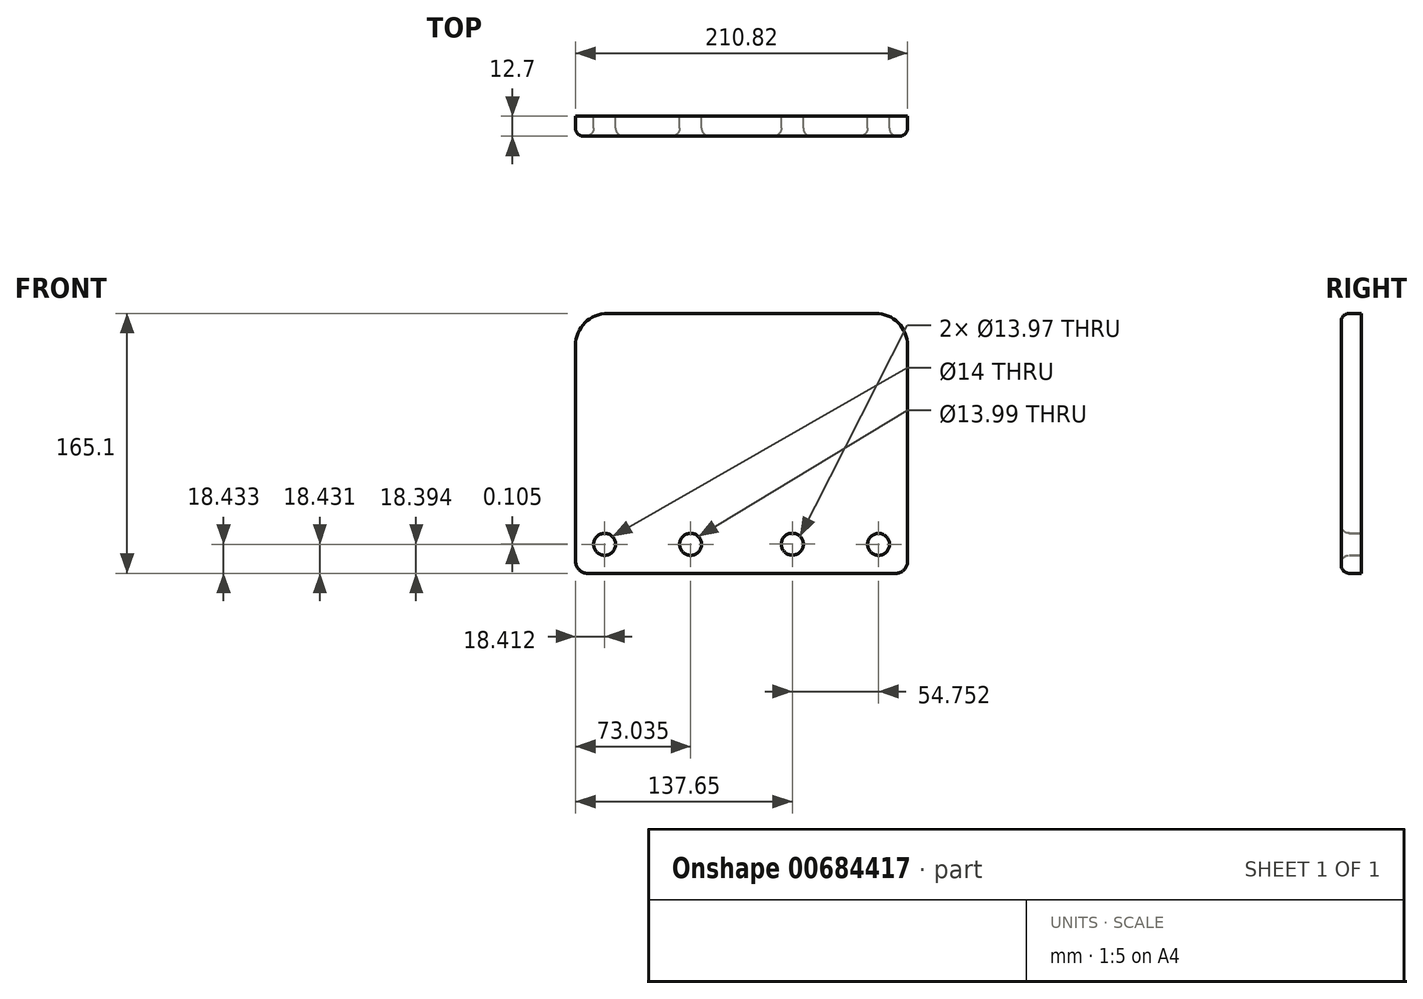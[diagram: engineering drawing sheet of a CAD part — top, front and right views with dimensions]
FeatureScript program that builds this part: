
annotation { "Feature Type Name" : "Feature", "Feature Type Description" : "" }
export const myFeature = defineFeature(function(context is Context, id is Id, definition is map)
    precondition{}
    {
        {
            var Q0;
            Q0=qCreatedBy(makeId("Front.planeOp"),FACE);
            var sketch = newSketch(context, id + "F0", { "sketchPlane" : qUnion([Q0])});
            skArc(sketch, "E0.7", {"start": v(-132.5, 111.2) * mm, "mid": v(-146.87, 105.25) * mm, "end": v(-152.82, 90.88) * mm});
            skLineSegment(sketch, "E0.8", {"start": v(-152.82, 90.88) * mm, "end": v(-152.82, -46.28) * mm});
            skLineSegment(sketch, "E0.9", {"start": v(-145.2, -53.9) * mm, "end": v(-55.03, -53.9) * mm});
            skArc(sketch, "E1.1", {"start": v(58, 90.88) * mm, "mid": v(52.05, 105.25) * mm, "end": v(37.68, 111.2) * mm});
            skLineSegment(sketch, "E1.2", {"start": v(58, -46.28) * mm, "end": v(58, 90.88) * mm});
            skLineSegment(sketch, "E1.3", {"start": v(-39.79, -53.9) * mm, "end": v(50.38, -53.9) * mm});
            skLineSegment(sketch, "E2", {"start": v(-55.03, -53.9) * mm, "end": v(-39.79, -53.9) * mm});
            skPoint(sketch, "E3.orphan", {"position": v(-98, 109.82) * mm});
            skLineSegment(sketch, "E4", {"start": v(21.17, 85.8) * mm, "end": v(21.17, 85.8) * mm});
            skLineSegment(sketch, "E5", {"start": v(-115.99, 85.8) * mm, "end": v(-115.99, 85.8) * mm});
            skPoint(sketch, "E6.visualSharp", {"position": v(-108.37, 111.2) * mm});
            skPoint(sketch, "E7.visualSharp", {"position": v(-108.37, 85.8) * mm});
            skPoint(sketch, "E8.newPointB", {"position": v(-121.07, 102.31) * mm});
            skPoint(sketch, "E9.visualSharp", {"position": v(13.55, 111.2) * mm});
            skPoint(sketch, "E10.orphan", {"position": v(26.25, 102.31) * mm});
            skPoint(sketch, "E11.visualSharp", {"position": v(13.55, 85.8) * mm});
            skPoint(sketch, "E12.visualSharp", {"position": v(26.25, 85.8) * mm});
            skPoint(sketch, "E13.visualSharp", {"position": v(-121.07, 35) * mm});
            skPoint(sketch, "E14.visualSharp", {"position": v(26.25, 35) * mm});
            skPoint(sketch, "E15", {"position": v(-47.4, 35) * mm});
            skPoint(sketch, "E16.visualSharp", {"position": v(-65.19, 35) * mm});
            skArc(sketch, "E16.filletArc", {"start": v(-65.05, 32.78) * mm, "mid": v(-65.9, 34.37) * mm, "end": v(-67.57, 35) * mm});
            skPoint(sketch, "E17.visualSharp", {"position": v(-29.63, 35) * mm});
            skArc(sketch, "E17.filletArc", {"start": v(-27.25, 35) * mm, "mid": v(-28.93, 34.37) * mm, "end": v(-29.77, 32.78) * mm});
            skPoint(sketch, "E18.visualSharp", {"position": v(-152.82, -53.9) * mm});
            skArc(sketch, "E18.filletArc", {"start": v(-152.82, -46.28) * mm, "mid": v(-150.59, -51.67) * mm, "end": v(-145.2, -53.9) * mm});
            skPoint(sketch, "E19.visualSharp", {"position": v(58, -53.9) * mm});
            skArc(sketch, "E19.filletArc", {"start": v(50.38, -53.9) * mm, "mid": v(55.77, -51.67) * mm, "end": v(58, -46.28) * mm});
            skCircle(sketch, "E20", {"center": v(-15.17, -35.4) * mm, "radius": 6.99 * mm});
            skCircle(sketch, "E21", {"center": v(39.58, -35.5) * mm, "radius": 6.99 * mm});
            skCircle(sketch, "E22", {"center": v(-134.4, -35.47) * mm, "radius": 7 * mm});
            skCircle(sketch, "E23", {"center": v(-79.78, -35.47) * mm, "radius": 7 * mm});
            skPoint(sketch, "E24.end.orphan", {"position": v(-113.45, 35) * mm});
            skPoint(sketch, "E14.filletArc.start.orphan", {"position": v(18.63, 35) * mm});
            skLineSegment(sketch, "E25", {"start": v(-132.5, 111.2) * mm, "end": v(37.68, 111.2) * mm});
            skSolve(sketch);
        }
        {
            var Q0;
            Q0=makeQuery(id+"F0.imprint","IMPRINT",FACE,{"disambiguationData":[TD([[makeQuery(id+"F0.imprint","IMPRINT",EDGE,{"derivedFrom":sQuery(id+"F0.wireOp",EDGE,"E0.7")}),1.0]])]});
            extrude(context, id + "F1", {"entities" : qUnion([Q0]), "depth" : 12.7 * mm, "offsetDistance" : 25.4 * mm});
        }
        {
            var Q0;
            Q0=makeQuery(id+"F1.opExtrude","CAP_FACE",FACE,{"disambiguationData":[OSD([sQuery(id+"F0.wireOp",EDGE,"E0.7"),sQuery(id+"F0.wireOp",EDGE,"E0.8"),sQuery(id+"F0.wireOp",EDGE,"E0.9"),sQuery(id+"F0.wireOp",EDGE,"E1.1"),sQuery(id+"F0.wireOp",EDGE,"E1.2"),sQuery(id+"F0.wireOp",EDGE,"E1.3"),sQuery(id+"F0.wireOp",EDGE,"E2"),sQuery(id+"F0.wireOp",EDGE,"E18.filletArc"),sQuery(id+"F0.wireOp",EDGE,"E19.filletArc"),sQuery(id+"F0.wireOp",EDGE,"E20"),sQuery(id+"F0.wireOp",EDGE,"E21"),sQuery(id+"F0.wireOp",EDGE,"E22"),sQuery(id+"F0.wireOp",EDGE,"E23"),sQuery(id+"F0.wireOp",EDGE,"E25")])],"isStart":false});
            fillet(context, id + "F2", {"entities" : qUnion([Q0]), "radius" : 5.08 * mm, "tangentPropagation" : true, "allowEdgeOverflow" : false});
        }
    });
